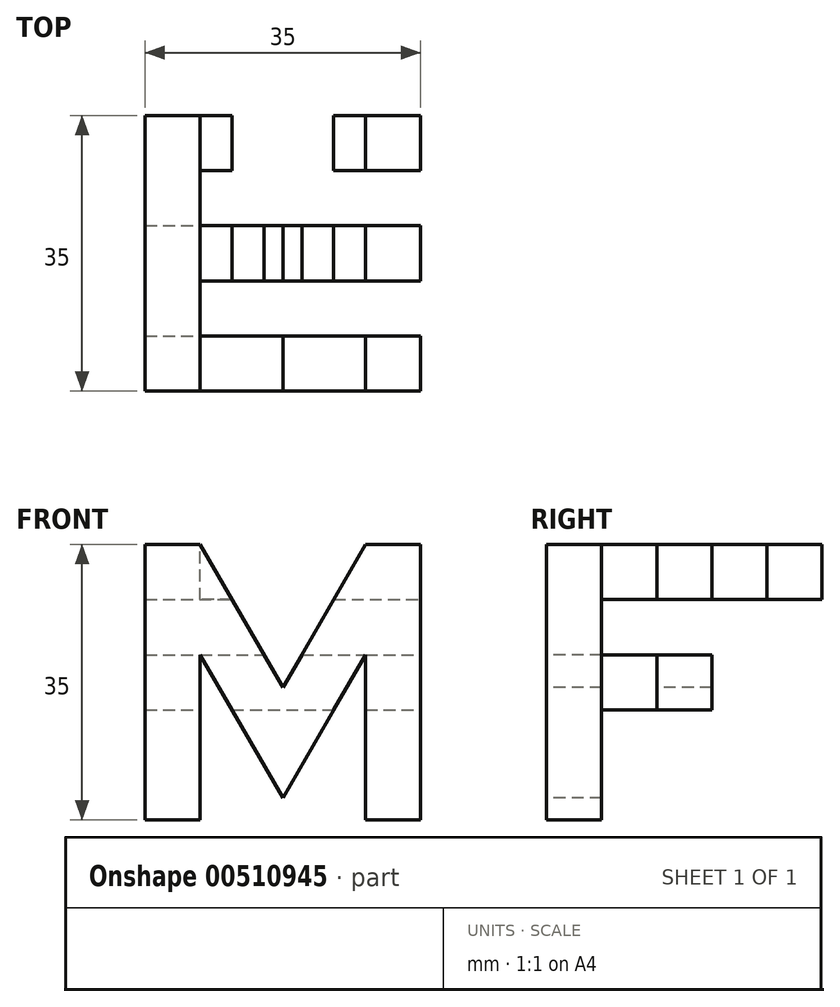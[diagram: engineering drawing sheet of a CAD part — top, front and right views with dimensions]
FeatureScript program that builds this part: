
annotation { "Feature Type Name" : "Feature", "Feature Type Description" : "" }
export const myFeature = defineFeature(function(context is Context, id is Id, definition is map)
    precondition{}
    {
        {
            var Q0;
            Q0=qCreatedBy(makeId("Top.planeOp"),FACE);
            var sketch = newSketch(context, id + "F0", { "sketchPlane" : qUnion([Q0])});
            skLineSegment(sketch, "E0.bottom", {"start": v(-17.5, -17.5) * mm, "end": v(17.5, -17.5) * mm});
            skLineSegment(sketch, "E0.top", {"start": v(-17.5, 17.5) * mm, "end": v(17.5, 17.5) * mm});
            skLineSegment(sketch, "E0.left", {"start": v(-17.5, -17.5) * mm, "end": v(-17.5, 17.5) * mm});
            skLineSegment(sketch, "E0.right", {"start": v(17.5, -17.5) * mm, "end": v(17.5, 17.5) * mm});
            skPoint(sketch, "E0.middle", {"position": v(0, 0) * mm});
            skSolve(sketch);
        }
        {
            var Q0;
            Q0=makeQuery(id+"F0.imprint","IMPRINT",FACE,{"disambiguationData":[TD([[makeQuery(id+"F0.imprint","IMPRINT",EDGE,{"derivedFrom":sQuery(id+"F0.wireOp",EDGE,"E0.bottom")}),1.0]])]});
            extrude(context, id + "F1", {"entities" : qUnion([Q0]), "depth" : 35 * mm});
        }
        {
            var Q0;
            Q0=makeQuery(id+"F1.opExtrude","CAP_FACE",FACE,{"disambiguationData":[OSD([sQuery(id+"F0.wireOp",EDGE,"E0.bottom"),sQuery(id+"F0.wireOp",EDGE,"E0.top"),sQuery(id+"F0.wireOp",EDGE,"E0.left"),sQuery(id+"F0.wireOp",EDGE,"E0.right")])],"isStart":false});
            var sketch = newSketch(context, id + "F2", { "sketchPlane" : qUnion([Q0])});
            skLineSegment(sketch, "E1.bottom", {"start": v(17.5, 17.5) * mm, "end": v(-17.5, 17.5) * mm});
            skLineSegment(sketch, "E1.top", {"start": v(17.5, 10.5) * mm, "end": v(-17.5, 10.5) * mm});
            skLineSegment(sketch, "E1.left", {"start": v(17.5, 17.5) * mm, "end": v(17.5, 10.5) * mm});
            skLineSegment(sketch, "E1.right", {"start": v(-17.5, 17.5) * mm, "end": v(-17.5, 10.5) * mm});
            skLineSegment(sketch, "E2.bottom", {"start": v(-17.5, -17.5) * mm, "end": v(-10.5, -17.5) * mm});
            skLineSegment(sketch, "E2.top", {"start": v(-17.5, 17.5) * mm, "end": v(-10.5, 17.5) * mm});
            skLineSegment(sketch, "E2.left", {"start": v(-17.5, -17.5) * mm, "end": v(-17.5, 17.5) * mm});
            skLineSegment(sketch, "E2.right", {"start": v(-10.5, -17.5) * mm, "end": v(-10.5, 17.5) * mm});
            skLineSegment(sketch, "E3.bottom", {"start": v(-17.5, 3.5) * mm, "end": v(17.5, 3.5) * mm});
            skLineSegment(sketch, "E3.top", {"start": v(-17.5, -3.5) * mm, "end": v(17.5, -3.5) * mm});
            skLineSegment(sketch, "E3.left", {"start": v(-17.5, 3.5) * mm, "end": v(-17.5, -3.5) * mm});
            skLineSegment(sketch, "E3.right", {"start": v(17.5, 3.5) * mm, "end": v(17.5, -3.5) * mm});
            skLineSegment(sketch, "E4.bottom", {"start": v(-17.5, -17.5) * mm, "end": v(17.5, -17.5) * mm});
            skLineSegment(sketch, "E4.top", {"start": v(-17.5, -10.5) * mm, "end": v(17.5, -10.5) * mm});
            skLineSegment(sketch, "E4.left", {"start": v(-17.5, -17.5) * mm, "end": v(-17.5, -10.5) * mm});
            skLineSegment(sketch, "E4.right", {"start": v(17.5, -17.5) * mm, "end": v(17.5, -10.5) * mm});
            skSolve(sketch);
        }
        {
            var Q0;
            Q0=makeQuery(id+"F1.opExtrude","SWEPT_FACE",FACE,{"disambiguationData":[OSD([sQuery(id+"F0.wireOp",EDGE,"E0.bottom")])]});
            var sketch = newSketch(context, id + "F3", { "sketchPlane" : qUnion([Q0])});
            skLineSegment(sketch, "E5.bottom", {"start": v(-17.5, 0) * mm, "end": v(-10.5, 0) * mm});
            skLineSegment(sketch, "E5.top", {"start": v(-17.5, 35) * mm, "end": v(-10.5, 35) * mm});
            skLineSegment(sketch, "E5.left", {"start": v(-17.5, 0) * mm, "end": v(-17.5, 35) * mm});
            skLineSegment(sketch, "E5.right", {"start": v(-10.5, 0) * mm, "end": v(-10.5, 35) * mm});
            skLineSegment(sketch, "E6.bottom", {"start": v(17.5, 0) * mm, "end": v(10.5, 0) * mm});
            skLineSegment(sketch, "E6.top", {"start": v(17.5, 35) * mm, "end": v(10.5, 35) * mm});
            skLineSegment(sketch, "E6.left", {"start": v(17.5, 0) * mm, "end": v(17.5, 35) * mm});
            skLineSegment(sketch, "E6.right", {"start": v(10.5, 0) * mm, "end": v(10.5, 35) * mm});
            skPoint(sketch, "E7", {"position": v(0, 16.81) * mm});
            skLineSegment(sketch, "E8", {"start": v(-10.5, 35) * mm, "end": v(0, 16.81) * mm});
            skLineSegment(sketch, "E9", {"start": v(0, 16.81) * mm, "end": v(10.5, 35) * mm});
            skLineSegment(sketch, "E10", {"start": v(0, 16.81) * mm, "end": v(0, 2.81) * mm});
            skLineSegment(sketch, "E11", {"start": v(0, 2.81) * mm, "end": v(-10.5, 21) * mm});
            skLineSegment(sketch, "E12", {"start": v(0, 2.81) * mm, "end": v(10.5, 21) * mm});
            skSolve(sketch);
        }
        {
            var Q0;
            Q0=makeQuery(id+"F1.opExtrude","SWEPT_FACE",FACE,{"disambiguationData":[OSD([sQuery(id+"F0.wireOp",EDGE,"E0.right")])]});
            var sketch = newSketch(context, id + "F4", { "sketchPlane" : qUnion([Q0])});
            skLineSegment(sketch, "E13.bottom", {"start": v(-17.5, 35) * mm, "end": v(17.5, 35) * mm});
            skLineSegment(sketch, "E13.top", {"start": v(-17.5, 28) * mm, "end": v(17.5, 28) * mm});
            skLineSegment(sketch, "E13.left", {"start": v(-17.5, 35) * mm, "end": v(-17.5, 28) * mm});
            skLineSegment(sketch, "E13.right", {"start": v(17.5, 35) * mm, "end": v(17.5, 28) * mm});
            skLineSegment(sketch, "E14.bottom", {"start": v(-17.5, 0) * mm, "end": v(-10.5, 0) * mm});
            skLineSegment(sketch, "E14.top", {"start": v(-17.5, 35) * mm, "end": v(-10.5, 35) * mm});
            skLineSegment(sketch, "E14.left", {"start": v(-17.5, 0) * mm, "end": v(-17.5, 35) * mm});
            skLineSegment(sketch, "E14.right", {"start": v(-10.5, 0) * mm, "end": v(-10.5, 35) * mm});
            skLineSegment(sketch, "E15.left", {"start": v(-17.5, 21) * mm, "end": v(-17.5, 14) * mm});
            skLineSegment(sketch, "E16.bottom", {"start": v(-17.5, 21) * mm, "end": v(3.5, 21) * mm});
            skLineSegment(sketch, "E16.top", {"start": v(-17.5, 14) * mm, "end": v(3.5, 14) * mm});
            skLineSegment(sketch, "E16.right", {"start": v(3.5, 21) * mm, "end": v(3.5, 14) * mm});
            skSolve(sketch);
        }
        {
            var Q0;
            {var subQ0=sQuery(id+"F2.wireOp",EDGE,"E1.top");var subQ3=sQuery(id+"F2.wireOp",EDGE,"E2.right");var subQ4=makeQuery(id+"F2.imprint","INTERSECT",VERTEX,{"derivedFrom":[subQ0,subQ3]});Q0=makeQuery(id+"F2.imprint","IMPRINT",FACE,{"disambiguationData":[TD([[makeQuery(id+"F2.imprint","IMPRINT",EDGE,{"disambiguationData":[TD([[subQ4,1.0]])],"derivedFrom":subQ3}),-1.0]])]});}
            extrude(context, id + "F5", {"entities" : qUnion([Q0]), "operationType" : NewBodyOperationType.REMOVE, "oppositeDirection" : true, "depth" : 35 * mm});
        }
        {
            var Q0;
            {var subQ0=sQuery(id+"F2.wireOp",EDGE,"E4.top");var subQ1=sQuery(id+"F2.wireOp",EDGE,"E2.right");var subQ2=makeQuery(id+"F2.imprint","INTERSECT",VERTEX,{"derivedFrom":[subQ1,subQ0]});Q0=makeQuery(id+"F2.imprint","IMPRINT",FACE,{"disambiguationData":[TD([[makeQuery(id+"F2.imprint","IMPRINT",EDGE,{"disambiguationData":[TD([[subQ2,-1.0]])],"derivedFrom":subQ1}),-1.0]])]});}
            extrude(context, id + "F6", {"entities" : qUnion([Q0]), "operationType" : NewBodyOperationType.REMOVE, "oppositeDirection" : true, "depth" : 35 * mm});
        }
        {
            var Q0;
            {var subQ0=sQuery(id+"F3.wireOp",EDGE,"E8");Q0=makeQuery(id+"F3.imprint","IMPRINT",FACE,{"disambiguationData":[TD([[makeQuery(id+"F3.imprint","IMPRINT",EDGE,{"derivedFrom":subQ0}),1.0]])]});}
            extrude(context, id + "F7", {"entities" : qUnion([Q0]), "operationType" : NewBodyOperationType.REMOVE, "oppositeDirection" : true, "depth" : 35 * mm});
        }
        {
            var Q0;
            {var subQ4=sQuery(id+"F3.wireOp",EDGE,"E11");Q0=makeQuery(id+"F3.imprint","IMPRINT",FACE,{"disambiguationData":[TD([[makeQuery(id+"F3.imprint","IMPRINT",EDGE,{"derivedFrom":subQ4}),1.0]])]});}
            extrude(context, id + "F8", {"entities" : qUnion([Q0]), "operationType" : NewBodyOperationType.REMOVE, "oppositeDirection" : true, "depth" : 35 * mm});
        }
        {
            var Q0;
            {var subQ5=sQuery(id+"F4.wireOp",EDGE,"E16.right");Q0=makeQuery(id+"F4.imprint","IMPRINT",FACE,{"disambiguationData":[TD([[makeQuery(id+"F4.imprint","IMPRINT",EDGE,{"derivedFrom":subQ5}),1.0]])]});}
            extrude(context, id + "F9", {"entities" : qUnion([Q0]), "operationType" : NewBodyOperationType.REMOVE, "oppositeDirection" : true, "depth" : 35 * mm});
        }
    });
